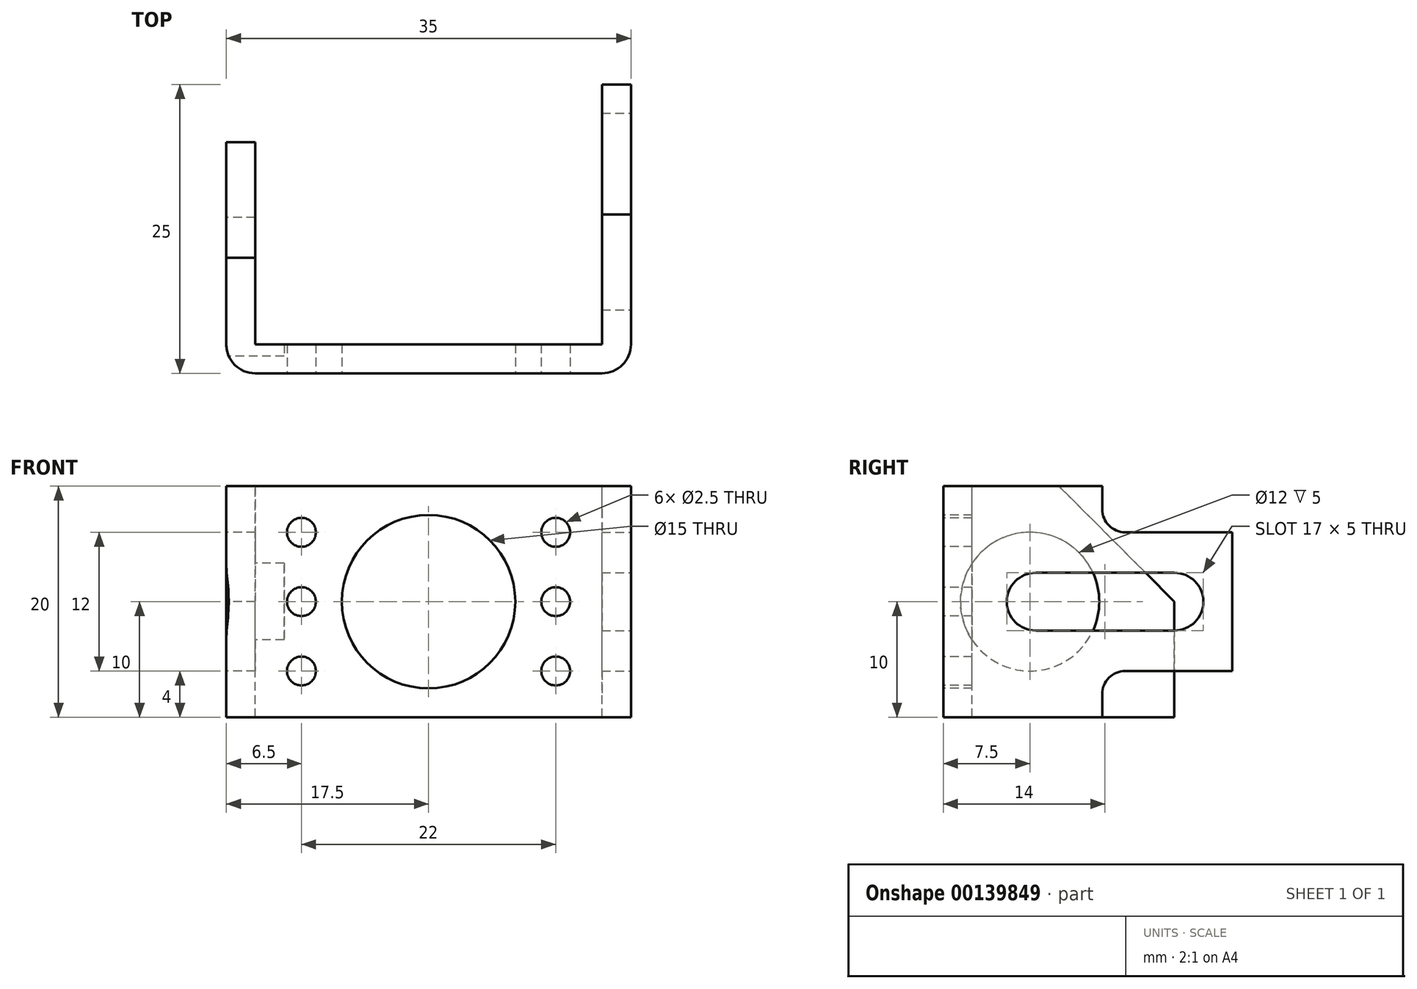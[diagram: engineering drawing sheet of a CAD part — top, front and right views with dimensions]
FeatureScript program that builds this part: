
annotation { "Feature Type Name" : "Feature", "Feature Type Description" : "" }
export const myFeature = defineFeature(function(context is Context, id is Id, definition is map)
    precondition{}
    {
        {
            var Q0;
            Q0=qCreatedBy(makeId("Top.planeOp"),FACE);
            var sketch = newSketch(context, id + "F0", { "sketchPlane" : qUnion([Q0])});
            skLineSegment(sketch, "E0.bottom", {"start": v(0, 0) * mm, "end": v(35, 0) * mm});
            skLineSegment(sketch, "E0.top", {"start": v(0, 20) * mm, "end": v(35, 20) * mm});
            skLineSegment(sketch, "E0.left", {"start": v(0, 0) * mm, "end": v(0, 20) * mm});
            skLineSegment(sketch, "E0.right", {"start": v(35, 0) * mm, "end": v(35, 20) * mm});
            skSolve(sketch);
        }
        {
            var Q0;
            Q0=makeQuery(id+"F0.imprint","IMPRINT",FACE,{"disambiguationData":[TD([[makeQuery(id+"F0.imprint","IMPRINT",EDGE,{"derivedFrom":sQuery(id+"F0.wireOp",EDGE,"E0.bottom")}),1.0]])]});
            extrude(context, id + "F1", {"entities" : qUnion([Q0]), "depth" : 20 * mm});
        }
        {
            var Q0;
            Q0=makeQuery(id+"F1.opExtrude","CAP_FACE",FACE,{"disambiguationData":[OSD([sQuery(id+"F0.wireOp",EDGE,"E0.bottom"),sQuery(id+"F0.wireOp",EDGE,"E0.top"),sQuery(id+"F0.wireOp",EDGE,"E0.left"),sQuery(id+"F0.wireOp",EDGE,"E0.right")])],"isStart":false});
            var sketch = newSketch(context, id + "F2", { "sketchPlane" : qUnion([Q0])});
            skLineSegment(sketch, "E1.bottom", {"start": v(2.5, 2.5) * mm, "end": v(32.5, 2.5) * mm});
            skLineSegment(sketch, "E1.top", {"start": v(2.5, 20) * mm, "end": v(32.5, 20) * mm});
            skLineSegment(sketch, "E1.left", {"start": v(2.5, 2.5) * mm, "end": v(2.5, 20) * mm});
            skLineSegment(sketch, "E1.right", {"start": v(32.5, 2.5) * mm, "end": v(32.5, 20) * mm});
            skSolve(sketch);
        }
        {
            var Q0;
            Q0=makeQuery(id+"F2.imprint","IMPRINT",FACE,{"disambiguationData":[TD([[makeQuery(id+"F2.imprint","IMPRINT",EDGE,{"derivedFrom":sQuery(id+"F2.wireOp",EDGE,"E1.bottom")}),1.0]])]});
            extrude(context, id + "F3", {"entities" : qUnion([Q0]), "operationType" : NewBodyOperationType.REMOVE, "oppositeDirection" : true, "depth" : 25 * mm});
        }
        {
            var Q0;
            Q0=makeQuery(id+"F1.opExtrude","SWEPT_FACE",FACE,{"disambiguationData":[OSD([sQuery(id+"F0.wireOp",EDGE,"E0.left")])]});
            var sketch = newSketch(context, id + "F4", { "sketchPlane" : qUnion([Q0])});
            skLineSegment(sketch, "E2", {"start": v(-20, 10) * mm, "end": v(-10, 20) * mm});
            skCircle(sketch, "E3", {"center": v(-7.5, 10) * mm, "radius": 6 * mm});
            skSolve(sketch);
        }
        {
            var Q0;
            Q0=makeQuery(id+"F4.imprint","IMPRINT",FACE,{"disambiguationData":[TD([[makeQuery(id+"F4.imprint","IMPRINT",EDGE,{"derivedFrom":sQuery(id+"F4.wireOp",EDGE,"E3")}),1.0]])]});
            var Q1;
            {var subQ0=sQuery(id+"F4.wireOp",EDGE,"E2");Q1=makeQuery(id+"F4.imprint","IMPRINT",FACE,{"disambiguationData":[TD([[makeQuery(id+"F4.imprint","IMPRINT",EDGE,{"derivedFrom":subQ0}),1.0]])]});}
            extrude(context, id + "F5", {"entities" : qUnion([Q0, Q1]), "operationType" : NewBodyOperationType.REMOVE, "oppositeDirection" : true, "depth" : 5 * mm});
        }
        {
            var Q0;
            Q0=makeQuery(id+"F1.opExtrude","SWEPT_EDGE",EDGE,{"disambiguationData":[OSD([sQuery(id+"F0.wireOp",EDGE,"E0.bottom"),sQuery(id+"F0.wireOp",EDGE,"E0.left")])]});
            var Q1;
            Q1=makeQuery(id+"F1.opExtrude","SWEPT_EDGE",EDGE,{"disambiguationData":[OSD([sQuery(id+"F0.wireOp",EDGE,"E0.bottom"),sQuery(id+"F0.wireOp",EDGE,"E0.right")])]});
            fillet(context, id + "F6", {"entities" : qUnion([Q0, Q1]), "radius" : 2.5 * mm, "tangentPropagation" : true, "allowEdgeOverflow" : false});
        }
        {
            var Q0;
            Q0=makeQuery(id+"F1.opExtrude","SWEPT_FACE",FACE,{"disambiguationData":[OSD([sQuery(id+"F0.wireOp",EDGE,"E0.bottom")])]});
            var sketch = newSketch(context, id + "F7", { "sketchPlane" : qUnion([Q0])});
            skLineSegment(sketch, "E4", {"start": v(17.5, 0) * mm, "end": v(17.5, 20) * mm, "construction": true});
            skCircle(sketch, "E5", {"center": v(17.5, 10) * mm, "radius": 7.5 * mm});
            skLineSegment(sketch, "E6", {"start": v(17.5, 10) * mm, "end": v(28.5, 10) * mm, "construction": true});
            skCircle(sketch, "E7", {"center": v(28.5, 10) * mm, "radius": 1.25 * mm});
            skCircle(sketch, "E8", {"center": v(28.5, 16) * mm, "radius": 1.25 * mm});
            skCircle(sketch, "E9", {"center": v(28.5, 4) * mm, "radius": 1.25 * mm});
            skSolve(sketch);
        }
        {
            var Q0;
            Q0=makeQuery(id+"F7.imprint","IMPRINT",FACE,{"disambiguationData":[TD([[makeQuery(id+"F7.imprint","IMPRINT",EDGE,{"derivedFrom":sQuery(id+"F7.wireOp",EDGE,"E5")}),1.0]])]});
            var Q1;
            Q1=makeQuery(id+"F7.imprint","IMPRINT",FACE,{"disambiguationData":[TD([[makeQuery(id+"F7.imprint","IMPRINT",EDGE,{"derivedFrom":sQuery(id+"F7.wireOp",EDGE,"E8")}),1.0]])]});
            var Q2;
            Q2=makeQuery(id+"F7.imprint","IMPRINT",FACE,{"disambiguationData":[TD([[makeQuery(id+"F7.imprint","IMPRINT",EDGE,{"derivedFrom":sQuery(id+"F7.wireOp",EDGE,"E7")}),1.0]])]});
            var Q3;
            Q3=makeQuery(id+"F7.imprint","IMPRINT",FACE,{"disambiguationData":[TD([[makeQuery(id+"F7.imprint","IMPRINT",EDGE,{"derivedFrom":sQuery(id+"F7.wireOp",EDGE,"E9")}),1.0]])]});
            extrude(context, id + "F8", {"entities" : qUnion([Q0, Q1, Q2, Q3]), "operationType" : NewBodyOperationType.REMOVE, "oppositeDirection" : true, "depth" : 25 * mm});
        }
        {
            var Q0;
            Q0=makeQuery(id+"F1.opExtrude","SWEPT_FACE",FACE,{"disambiguationData":[OSD([sQuery(id+"F0.wireOp",EDGE,"E0.bottom")])]});
            var sketch = newSketch(context, id + "F9", { "sketchPlane" : qUnion([Q0])});
            skLineSegment(sketch, "E10", {"start": v(17.5, 0) * mm, "end": v(17.5, 20) * mm, "construction": true});
            skLineSegment(sketch, "E11", {"start": v(17.5, 10) * mm, "end": v(6.5, 10) * mm, "construction": true});
            skCircle(sketch, "E12", {"center": v(6.5, 10) * mm, "radius": 1.25 * mm});
            skLineSegment(sketch, "E13", {"start": v(6.5, 10) * mm, "end": v(6.5, 16) * mm, "construction": true});
            skCircle(sketch, "E14", {"center": v(6.5, 16) * mm, "radius": 1.25 * mm});
            skLineSegment(sketch, "E15", {"start": v(6.5, 10) * mm, "end": v(6.5, 4) * mm, "construction": true});
            skCircle(sketch, "E16", {"center": v(6.5, 4) * mm, "radius": 1.25 * mm});
            skSolve(sketch);
        }
        {
            var Q0;
            Q0=makeQuery(id+"F9.imprint","IMPRINT",FACE,{"disambiguationData":[TD([[makeQuery(id+"F9.imprint","IMPRINT",EDGE,{"derivedFrom":sQuery(id+"F9.wireOp",EDGE,"E16")}),1.0]])]});
            var Q1;
            Q1=makeQuery(id+"F9.imprint","IMPRINT",FACE,{"disambiguationData":[TD([[makeQuery(id+"F9.imprint","IMPRINT",EDGE,{"derivedFrom":sQuery(id+"F9.wireOp",EDGE,"E12")}),1.0]])]});
            var Q2;
            Q2=makeQuery(id+"F9.imprint","IMPRINT",FACE,{"disambiguationData":[TD([[makeQuery(id+"F9.imprint","IMPRINT",EDGE,{"derivedFrom":sQuery(id+"F9.wireOp",EDGE,"E14")}),1.0]])]});
            extrude(context, id + "F10", {"entities" : qUnion([Q0, Q1, Q2]), "operationType" : NewBodyOperationType.REMOVE, "oppositeDirection" : true, "depth" : 25 * mm});
        }
        {
            var Q0;
            {var subQ0=sQuery(id+"F0.wireOp",EDGE,"E0.right");var subQ2=sQuery(id+"F0.wireOp",EDGE,"E0.top");Q0=makeQuery(id+"F3.boolean.opBoolean","SPLIT",FACE,{"disambiguationData":[TD([makeQuery(id+"F1.opExtrude","SWEPT_FACE",FACE,{"disambiguationData":[OSD([subQ0])]})])],"derivedFrom":makeQuery(id+"F1.opExtrude","SWEPT_FACE",FACE,{"disambiguationData":[OSD([subQ2])]})});}
            extrude(context, id + "F11", {"entities" : qUnion([Q0]), "operationType" : NewBodyOperationType.ADD, "depth" : 5 * mm});
        }
        {
            var Q0;
            {var subQ0=sQuery(id+"F0.wireOp",EDGE,"E0.right");Q0=makeQuery(id+"F11.boolean.opBoolean","MERGE",FACE,{"derivedFrom":[makeQuery(id+"F1.opExtrude","SWEPT_FACE",FACE,{"disambiguationData":[OSD([subQ0])]}),makeQuery(id+"F11.opExtrude","SWEPT_FACE",FACE,{"disambiguationData":[OSD([sQuery(id+"F0.wireOp",EDGE,"E0.top"),subQ0])]})]});}
            var sketch = newSketch(context, id + "F12", { "sketchPlane" : qUnion([Q0])});
            skLineSegment(sketch, "E17", {"start": v(25, 10) * mm, "end": v(20, 10) * mm, "construction": true});
            skPoint(sketch, "E17.endSnap0", {"position": v(25, 10) * mm});
            skLineSegment(sketch, "E18", {"start": v(20, 10) * mm, "end": v(8, 10) * mm, "construction": true});
            skPoint(sketch, "E18.endSnap0", {"position": v(2.5, 10) * mm});
            skArc(sketch, "E19", {"start": v(20, 7.5) * mm, "mid": v(22.5, 10) * mm, "end": v(20, 12.5) * mm});
            skArc(sketch, "E20", {"start": v(8, 12.5) * mm, "mid": v(5.5, 10) * mm, "end": v(8, 7.5) * mm});
            skLineSegment(sketch, "E21", {"start": v(8, 7.5) * mm, "end": v(20, 7.5) * mm});
            skLineSegment(sketch, "E22", {"start": v(20, 12.5) * mm, "end": v(8, 12.5) * mm});
            skLineSegment(sketch, "E23", {"start": v(13.75, 0) * mm, "end": v(13.75, 20) * mm, "construction": true});
            skLineSegment(sketch, "E24", {"start": v(25, 4) * mm, "end": v(13.75, 4) * mm});
            skLineSegment(sketch, "E25", {"start": v(25, 16) * mm, "end": v(13.75, 16) * mm});
            skArc(sketch, "E26", {"start": v(15.75, 4) * mm, "mid": v(14.34, 3.41) * mm, "end": v(13.75, 2) * mm});
            skArc(sketch, "E27", {"start": v(13.75, 18) * mm, "mid": v(14.34, 16.59) * mm, "end": v(15.75, 16) * mm});
            skLineSegment(sketch, "E28", {"start": v(13.75, 0) * mm, "end": v(13.75, 2) * mm});
            skLineSegment(sketch, "E29", {"start": v(13.75, 18) * mm, "end": v(13.75, 20) * mm});
            skSolve(sketch);
        }
        {
            var Q0;
            Q0=makeQuery(id+"F12.imprint","IMPRINT",FACE,{"disambiguationData":[TD([[makeQuery(id+"F12.imprint","IMPRINT",EDGE,{"derivedFrom":sQuery(id+"F12.wireOp",EDGE,"E19")}),1.0]])]});
            var Q1;
            {var subQ8=sQuery(id+"F12.wireOp",EDGE,"E27");Q1=makeQuery(id+"F12.imprint","IMPRINT",FACE,{"disambiguationData":[TD([[makeQuery(id+"F12.imprint","IMPRINT",EDGE,{"derivedFrom":subQ8}),1.0]])]});}
            var Q2;
            {var subQ8=sQuery(id+"F12.wireOp",EDGE,"E26");Q2=makeQuery(id+"F12.imprint","IMPRINT",FACE,{"disambiguationData":[TD([[makeQuery(id+"F12.imprint","IMPRINT",EDGE,{"derivedFrom":subQ8}),1.0]])]});}
            extrude(context, id + "F13", {"entities" : qUnion([Q0, Q1, Q2]), "operationType" : NewBodyOperationType.REMOVE, "oppositeDirection" : true, "depth" : 5 * mm});
        }
    });
